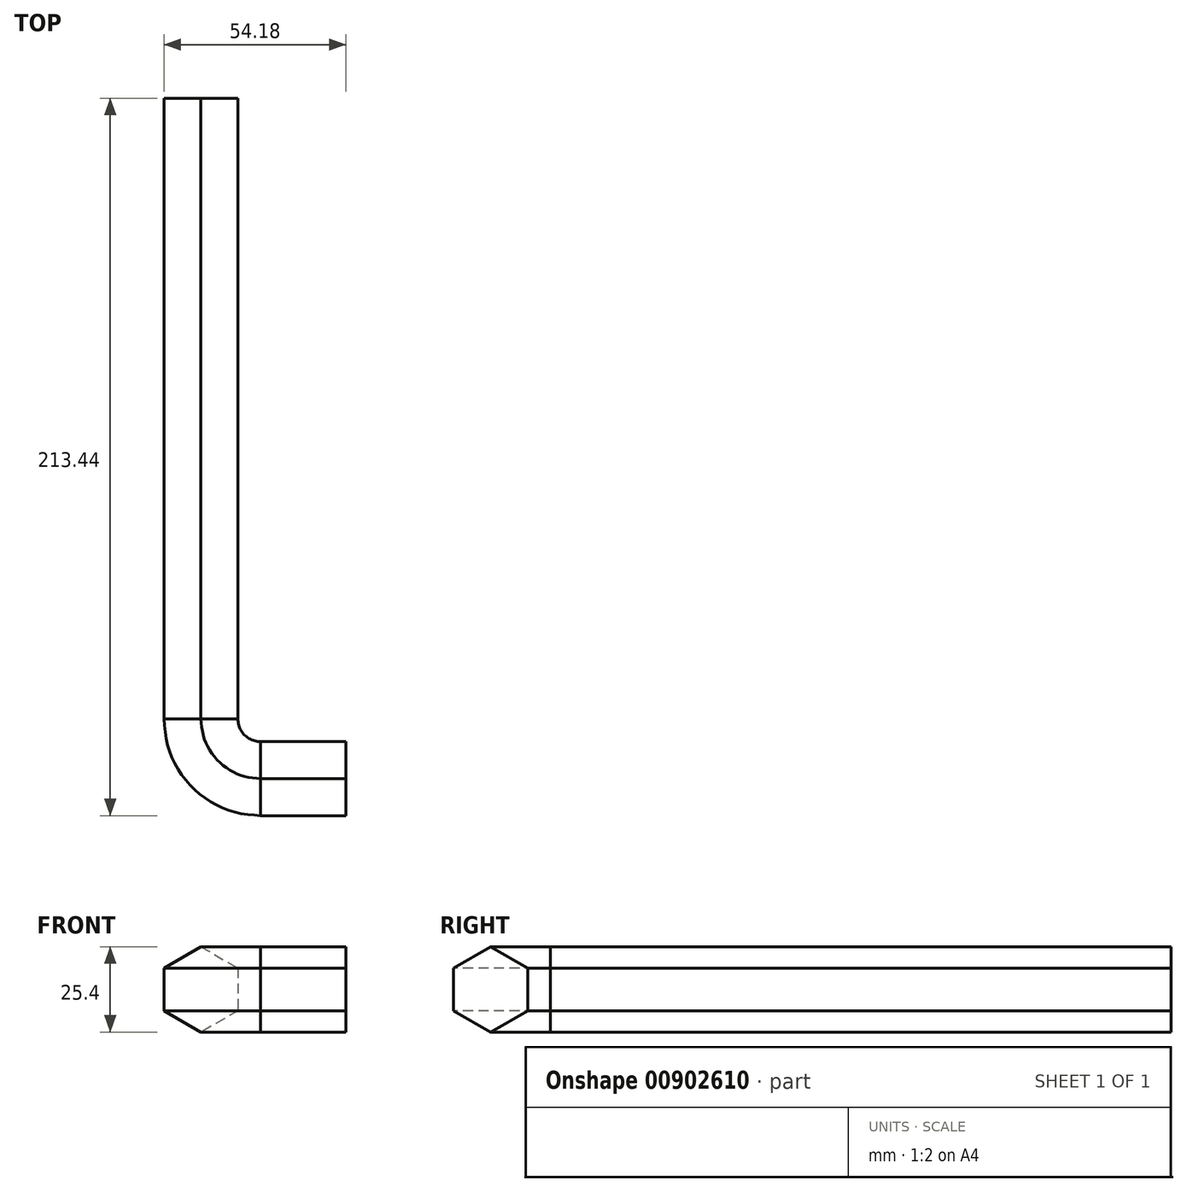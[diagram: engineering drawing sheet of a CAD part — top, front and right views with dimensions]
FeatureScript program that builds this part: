
annotation { "Feature Type Name" : "Feature", "Feature Type Description" : "" }
export const myFeature = defineFeature(function(context is Context, id is Id, definition is map)
    precondition{}
    {
        {
            var Q0;
            Q0=qCreatedBy(makeId("Front.planeOp"),FACE);
            var sketch = newSketch(context, id + "F0", { "sketchPlane" : qUnion([Q0])});
            skCircle(sketch, "E0.cCircle", {"center": v(-17.78, 0) * mm, "radius": 11 * mm, "construction": true});
            skLineSegment(sketch, "E0.0", {"start": v(-6.78, 6.35) * mm, "end": v(-6.78, -6.35) * mm});
            skLineSegment(sketch, "E0.1", {"start": v(-6.78, -6.35) * mm, "end": v(-17.78, -12.7) * mm});
            skLineSegment(sketch, "E0.2", {"start": v(-17.78, -12.7) * mm, "end": v(-28.78, -6.35) * mm});
            skLineSegment(sketch, "E0.3", {"start": v(-28.78, -6.35) * mm, "end": v(-28.78, 6.35) * mm});
            skLineSegment(sketch, "E0.4", {"start": v(-28.78, 6.35) * mm, "end": v(-17.78, 12.7) * mm});
            skLineSegment(sketch, "E0.5", {"start": v(-17.78, 12.7) * mm, "end": v(-6.78, 6.35) * mm});
            skPoint(sketch, "E0.0.midPoint", {"position": v(-6.78, 0) * mm});
            skSolve(sketch);
        }
        {
            var Q0;
            Q0=qCreatedBy(makeId("Right.planeOp"),FACE);
            var sketch = newSketch(context, id + "F1", { "sketchPlane" : qUnion([Q0])});
            skCircle(sketch, "E1.cCircle", {"center": v(-17.78, 0) * mm, "radius": 11 * mm, "construction": true});
            skLineSegment(sketch, "E1.0", {"start": v(-17.78, 12.7) * mm, "end": v(-6.78, 6.35) * mm});
            skLineSegment(sketch, "E1.1", {"start": v(-6.78, 6.35) * mm, "end": v(-6.78, -6.35) * mm});
            skLineSegment(sketch, "E1.2", {"start": v(-6.78, -6.35) * mm, "end": v(-17.78, -12.7) * mm});
            skLineSegment(sketch, "E1.3", {"start": v(-17.78, -12.7) * mm, "end": v(-28.78, -6.35) * mm});
            skLineSegment(sketch, "E1.4", {"start": v(-28.78, -6.35) * mm, "end": v(-28.78, 6.35) * mm});
            skLineSegment(sketch, "E1.5", {"start": v(-28.78, 6.35) * mm, "end": v(-17.78, 12.7) * mm});
            skPoint(sketch, "E1.0.midPoint", {"position": v(-12.28, 9.52) * mm});
            skSolve(sketch);
        }
        {
            var Q0;
            Q0=qCreatedBy(makeId("Top.planeOp"),FACE);
            var sketch = newSketch(context, id + "F2", { "sketchPlane" : qUnion([Q0])});
            skArc(sketch, "E2", {"start": v(-17.78, 0) * mm, "mid": v(-12.6, -12.6) * mm, "end": v(0, -17.78) * mm});
            skSolve(sketch);
        }
        {
            var Q0;
            Q0=sQuery(id+"F2.wireOp",EDGE,"E2");
            var Q1;
            Q1=makeQuery(id+"F0.imprint","IMPRINT",FACE,{"disambiguationData":[TD([[makeQuery(id+"F0.imprint","IMPRINT",EDGE,{"derivedFrom":sQuery(id+"F0.wireOp",EDGE,"E0.0")}),-1.0]])]});
            var Q2;
            Q2=makeQuery(id+"F1.imprint","IMPRINT",FACE,{"disambiguationData":[TD([[makeQuery(id+"F1.imprint","IMPRINT",EDGE,{"derivedFrom":sQuery(id+"F1.wireOp",EDGE,"E1.0")}),-1.0]])]});
            loft(context, id + "F3", {"addSections" : true, "spine" : qUnion([Q0]), "sectionCount" : 5, "sheetProfilesArray" : [{ "sheetProfileEntities" : qUnion([Q1]) }, { "sheetProfileEntities" : qUnion([Q2]) }]});
        }
        {
            var Q0;
            Q0=makeQuery(id+"F1.imprint","IMPRINT",FACE,{"disambiguationData":[TD([[makeQuery(id+"F1.imprint","IMPRINT",EDGE,{"derivedFrom":sQuery(id+"F1.wireOp",EDGE,"E1.0")}),-1.0]])]});
            extrude(context, id + "F4", {"entities" : qUnion([Q0]), "operationType" : NewBodyOperationType.ADD, "depth" : 25.4 * mm, "offsetDistance" : 25.4 * mm});
        }
        {
            var Q0;
            Q0=makeQuery(id+"F0.imprint","IMPRINT",FACE,{"disambiguationData":[TD([[makeQuery(id+"F0.imprint","IMPRINT",EDGE,{"derivedFrom":sQuery(id+"F0.wireOp",EDGE,"E0.0")}),-1.0]])]});
            extrude(context, id + "F5", {"entities" : qUnion([Q0]), "operationType" : NewBodyOperationType.ADD, "oppositeDirection" : true, "depth" : 184.66 * mm, "offsetDistance" : 25.4 * mm});
        }
    });
